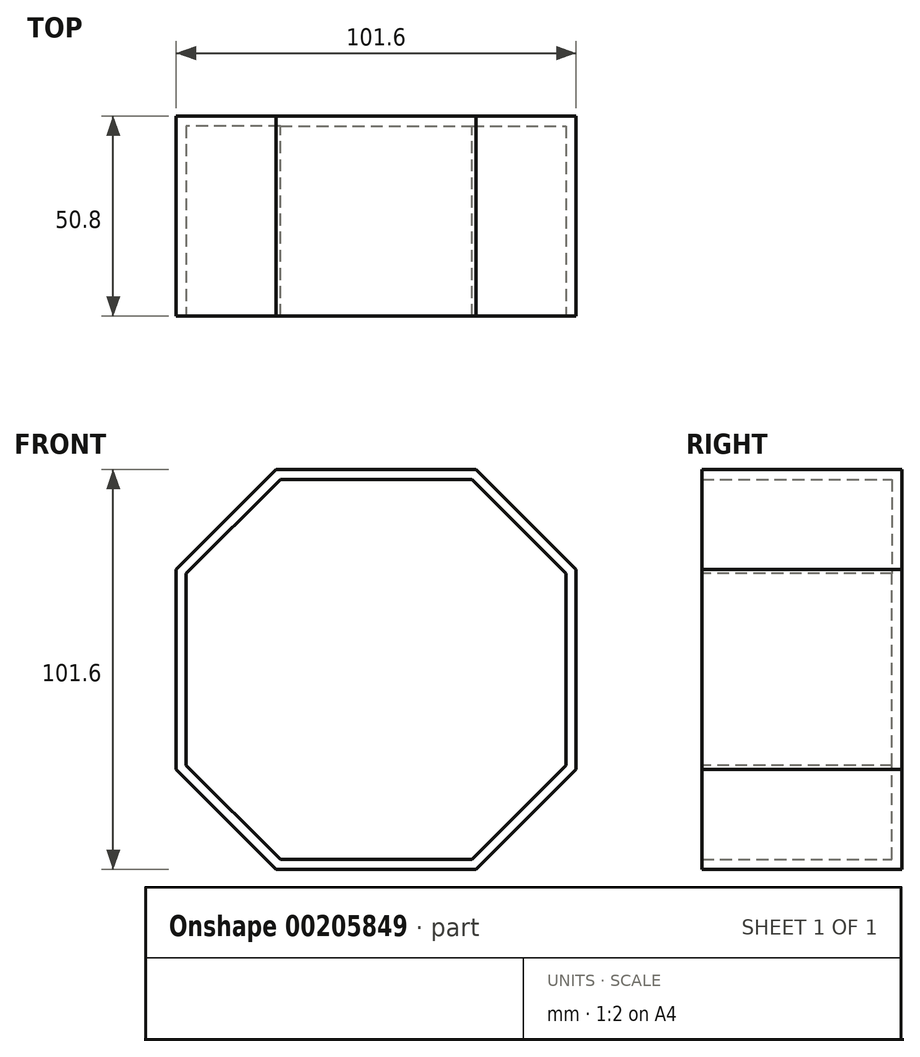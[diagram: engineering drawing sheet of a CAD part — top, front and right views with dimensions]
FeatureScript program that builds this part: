
annotation { "Feature Type Name" : "Feature", "Feature Type Description" : "" }
export const myFeature = defineFeature(function(context is Context, id is Id, definition is map)
    precondition{}
    {
        {
            var Q0;
            Q0=qCreatedBy(makeId("Front.planeOp"),FACE);
            var sketch = newSketch(context, id + "F0", { "sketchPlane" : qUnion([Q0])});
            skLineSegment(sketch, "E0.bottom", {"start": v(-50.8, -50.8) * mm, "end": v(50.8, -50.8) * mm});
            skLineSegment(sketch, "E0.top", {"start": v(-50.8, 50.8) * mm, "end": v(50.8, 50.8) * mm});
            skLineSegment(sketch, "E0.left", {"start": v(-50.8, -50.8) * mm, "end": v(-50.8, 50.8) * mm});
            skLineSegment(sketch, "E0.right", {"start": v(50.8, -50.8) * mm, "end": v(50.8, 50.8) * mm});
            skPoint(sketch, "E0.middle", {"position": v(0, 0) * mm});
            skSolve(sketch);
        }
        {
            var Q0;
            Q0=makeQuery(id+"F0.imprint","IMPRINT",FACE,{"disambiguationData":[TD([[makeQuery(id+"F0.imprint","IMPRINT",EDGE,{"derivedFrom":sQuery(id+"F0.wireOp",EDGE,"E0.bottom")}),1.0]])]});
            extrude(context, id + "F1", {"entities" : qUnion([Q0]), "endBound" : BoundingType.SYMMETRIC, "depth" : 50.8 * mm, "offsetDistance" : 25.4 * mm});
        }
        {
            var Q0;
            Q0=makeQuery(id+"F1.opExtrude","SWEPT_EDGE",EDGE,{"disambiguationData":[OSD([sQuery(id+"F0.wireOp",EDGE,"E0.top"),sQuery(id+"F0.wireOp",EDGE,"E0.left")])]});
            var Q1;
            Q1=makeQuery(id+"F1.opExtrude","SWEPT_EDGE",EDGE,{"disambiguationData":[OSD([sQuery(id+"F0.wireOp",EDGE,"E0.top"),sQuery(id+"F0.wireOp",EDGE,"E0.right")])]});
            var Q2;
            Q2=makeQuery(id+"F1.opExtrude","SWEPT_EDGE",EDGE,{"disambiguationData":[OSD([sQuery(id+"F0.wireOp",EDGE,"E0.bottom"),sQuery(id+"F0.wireOp",EDGE,"E0.left")])]});
            var Q3;
            Q3=makeQuery(id+"F1.opExtrude","SWEPT_EDGE",EDGE,{"disambiguationData":[OSD([sQuery(id+"F0.wireOp",EDGE,"E0.bottom"),sQuery(id+"F0.wireOp",EDGE,"E0.right")])]});
            chamfer(context, id + "F2", {"entities" : qUnion([Q0, Q1, Q2, Q3]), "width" : 25.4 * mm, "tangentPropagation" : true});
        }
        {
            var Q0;
            Q0=makeQuery(id+"F1.opExtrude","CAP_FACE",FACE,{"disambiguationData":[OSD([sQuery(id+"F0.wireOp",EDGE,"E0.bottom"),sQuery(id+"F0.wireOp",EDGE,"E0.top"),sQuery(id+"F0.wireOp",EDGE,"E0.left"),sQuery(id+"F0.wireOp",EDGE,"E0.right")])],"isStart":false});
            shell(context, id + "F3", {"entities" : qUnion([Q0]), "thickness" : 2.54 * mm});
        }
    });
